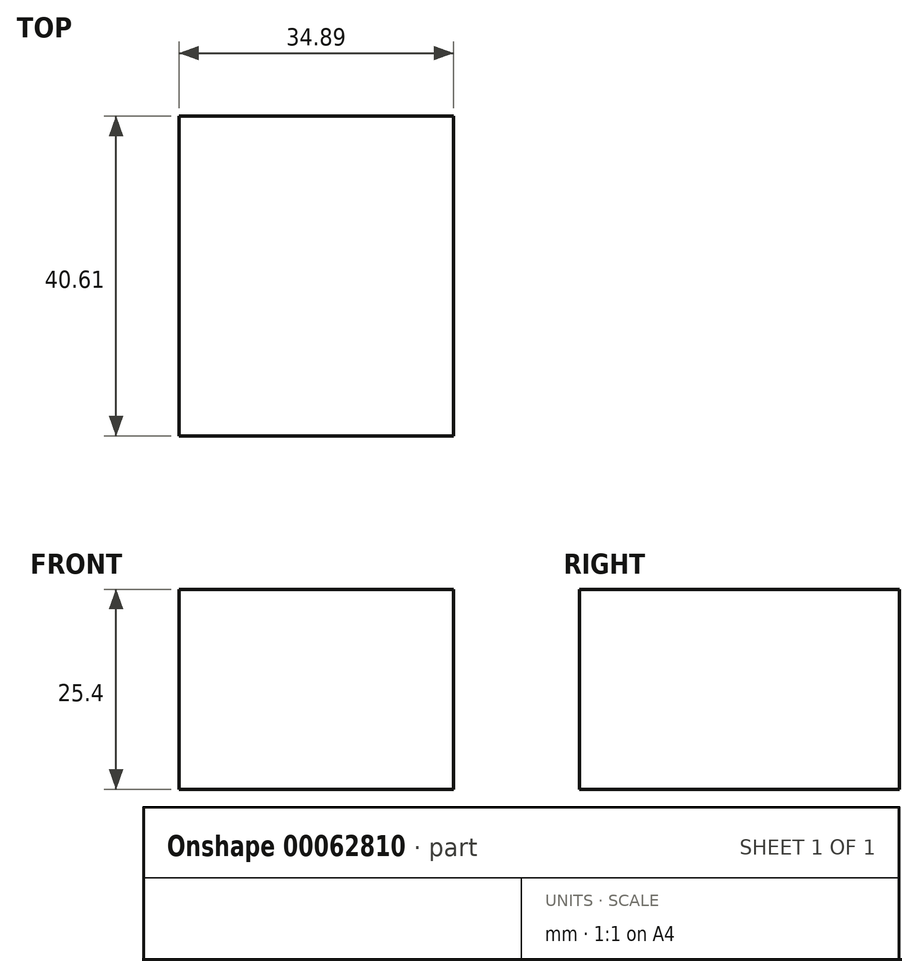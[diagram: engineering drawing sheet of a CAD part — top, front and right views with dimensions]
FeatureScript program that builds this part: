
annotation { "Feature Type Name" : "Feature", "Feature Type Description" : "" }
export const myFeature = defineFeature(function(context is Context, id is Id, definition is map)
    precondition{}
    {
        {
            var Q0;
            Q0=qCreatedBy(makeId("Top.planeOp"),FACE);
            var sketch = newSketch(context, id + "F0", { "sketchPlane" : qUnion([Q0])});
            skLineSegment(sketch, "E0.bottom", {"start": v(-70, -31.2) * mm, "end": v(-35.11, -31.2) * mm});
            skLineSegment(sketch, "E0.top", {"start": v(-70, 9.4) * mm, "end": v(-35.11, 9.4) * mm});
            skLineSegment(sketch, "E0.left", {"start": v(-70, -31.2) * mm, "end": v(-70, 9.4) * mm});
            skLineSegment(sketch, "E0.right", {"start": v(-35.11, -31.2) * mm, "end": v(-35.11, 9.4) * mm});
            skSolve(sketch);
        }
        {
            var Q0;
            Q0 = qSketchRegion(id + "F0", true);
            extrude(context, id + "F1", {"entities" : qUnion([Q0]), "depth" : 25.4 * mm});
        }
    });
